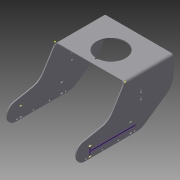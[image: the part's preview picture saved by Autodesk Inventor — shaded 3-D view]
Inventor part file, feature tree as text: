
AUTODESK INVENTOR PART (.ipt)
format: ipt  version: 2015 (Build 190159000, 159)  size: 395,776 bytes
history: native  units: mm
features: sketch x5, other x2, extrude x1
ambient origin geometry x8: Origin, YZ Plane, XZ Plane, XY Plane, X Axis, Y Axis, Z Axis, Center Point
bodies: Body1 (feature_tree)
feature tree (8):
  extrude  "Extrusion25"  Depth=3.0mm TaperAngle=0.0deg
  other  "Bend Part37"
  other  "Bend Part38"
  sketch  "Sketch47"  dims[d813=5.0mm d814=90.0deg]
  sketch  "Sketch48"
  sketch  "Sketch44"  dims[d19=5.0mm d127=97.0mm d151=5.0mm d163=5.0mm d222=5.0mm d248=40.0mm d294=25.0mm d324=5.0mm d326=25.0mm d329=25.0mm d344=6.0mm d358=6.0mm d404=5.0mm d406=45.0mm d445=20.0mm d446=30.0mm d448=45.0deg d460=5.606189mm d463=30.0deg d467=42.0mm d468=36.0mm d469=150.0deg d483=12.0mm d486=42.0mm d487=150.0deg d488=36.0mm d489=150.0deg d528=20.0mm d530=65.0mm]
  sketch  "Sketch45"  dims[d726=80.0mm d727=50.0mm d728=200.0mm d729=100.0mm d730=70.0mm d731=180.0mm d732=20.0mm d733=100.0mm d734=50.0mm d735=50.0mm d736=25.0mm d737=5.0mm d738=5.0mm d739=150.0mm d740=5.0mm d741=5.0mm d742=30.0mm d743=10.0mm d744=6.0mm d745=97.0mm d746=73.0mm d747=4.0mm d748=8.0mm d749=8.0mm d750=7.0mm d751=4.0mm d752=8.0mm d753=8.0mm d754=1.0mm d755=8.0mm d756=4.0mm d757=7.0mm d758=8.0mm d759=4.0mm d760=8.0mm d761=30.0mm d762=8.0mm d763=1.0mm d764=30.0mm d765=8.0mm d766=4.0mm d767=8.0mm d768=4.0mm d769=30.0mm d770=7.0mm d771=5.0mm d772=8.0mm d773=4.0mm d774=8.0mm d775=4.0mm d776=30.0mm d777=7.0mm d778=5.0mm d779=90.0mm d780=97.0mm d781=6.0mm d782=10.0mm d783=73.0mm d784=65.0mm d785=100.0mm d786=200.0mm d787=5.0mm d788=2.5mm d789=50.0mm d790=2.5mm d791=5.0mm d792=5.0mm d793=50.0mm d794=5.0mm d795=5.0mm d796=50.0mm d797=5.0mm d798=5.0mm d799=50.0mm d800=5.0mm d801=5.0mm d802=50.0mm d803=10.0mm d804=6.0mm d805=10.0mm d806=10.0mm d807=10.0mm d808=6.0mm d809=3.0mm d810=0.0mm]
  sketch  "Sketch46"  dims[d811=5.0mm d812=90.0deg]
